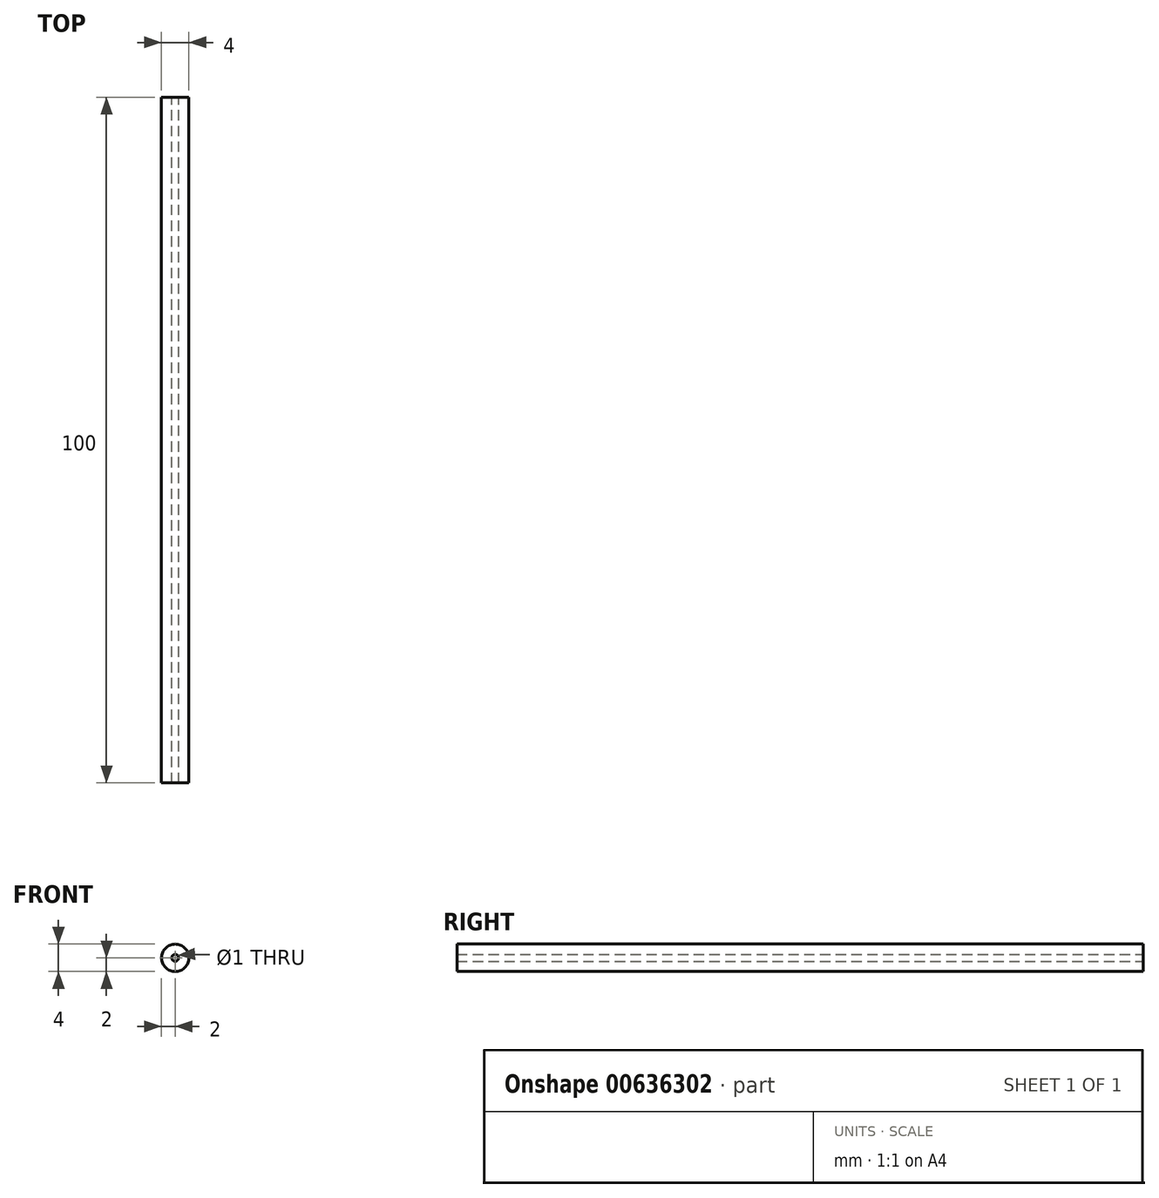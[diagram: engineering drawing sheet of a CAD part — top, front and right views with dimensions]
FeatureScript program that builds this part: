
annotation { "Feature Type Name" : "Feature", "Feature Type Description" : "" }
export const myFeature = defineFeature(function(context is Context, id is Id, definition is map)
    precondition{}
    {
        {
            var Q0;
            Q0=qCreatedBy(makeId("Front.planeOp"),FACE);
            var sketch = newSketch(context, id + "F0", { "sketchPlane" : qUnion([Q0])});
            skCircle(sketch, "E0", {"center": v(0, 0) * mm, "radius": 2 * mm});
            skSolve(sketch);
        }
        {
            var Q0;
            Q0 = qSketchRegion(id + "F0", true);
            extrude(context, id + "F1", {"entities" : qUnion([Q0]), "depth" : 100 * mm, "offsetDistance" : 25 * mm});
        }
        {
            var Q0;
            Q0=sQuery(id+"F0.wireOp",VERTEX,"E0.center");
            var Q1;
            Q1=makeQuery(id+"F1.opExtrude","SWEPT_BODY",BODY,{"disambiguationData":[OSD([sQuery(id+"F0.wireOp",EDGE,"E0")])]});
            hole(context, id + "F2", {"style" : HoleStyle.SIMPLE, "endStyle" : HoleEndStyle.THROUGH, "oppositeDirection" : true, "holeDiameter" : 1 * mm, "majorDiameter" : 5 * mm, "isTappedThrough" : true, "tappedDepth" : 12 * mm, "tapClearance" : 3, "locations" : qUnion([Q0]), "scope" : qUnion([Q1])});
        }
    });
